# Revit family: LA2C-Fork
name_source: partatom
category: Lighting Fixtures
revit_build: Autodesk Revit 2014 (Build: 20130709_2115(x64)
units: mm (PartAtom-declared; Revit-internal decimal feet)

## types (1)
- Fork
    Color Filter = 16777215
    Comments = This model is for use in spatial massing and rendering. Please contact LightArt for pick-point placement and installation details.
    Description = 22w
    Diffuser = White Opal Acrylic
    Dimming Compatibility = 0-10v
    Dimming Lamp Color Temperature Shift = <None>
    Driver = 24v
    HARDWARE_2 = Removable powder coated lid
Stainless steel canopy mounts to
standard junction box (provided by others)
(3-4) 3/64” stainless steel cables to canopy
Silver power cord to canopy
Adjustable 24”-96” suspension
    Hardware = Stainless Steel Cables
    Height = 8 "
    Height From Face = 50 "
    Input = 120v-277v
    LIGHTING = Solid State LED System
120v-277v input; 24v driver;
0-10v dimming compatible
3000k 81 CRI light source
S - 22w, 1050mA, 1045 lumens
    Light Source Symbol Size = 6 "
    Manufacturer = LightArt
    Model = LA2C
    STANDARDS = Damp Rated
3-6 week lead time, CSA Approved to UL standards
    Shade = 3form Varia Ecoresin
    Type Comments = Stainless steel canopy mounts to
standard junction box (provided by others)
    Wattage Comments = 14
    Weight = 9 lbs

## geometry (parser evidence)
native form markers: Sweep x26
no freeform markers — native parametric forms only
